FCSTD DOCUMENT  (FreeCAD 0.18R16146 (Git))
Label: main
License: All rights reserved
LicenseURL: http://en.wikipedia.org/wiki/All_rights_reserved
objects: Part::Feature×19, Part::Cylinder×14, Part::Cut×13, Part::Chamfer×7, Part::MultiFuse×2, Part::Box×2
note: 57 computed .brp shape members not serialized (recipe doc carries the construction recipe); baked Part::Feature solids carry a one-line shape summary decoded from their .brp

FEATURE [Part::Feature] Part__Feature071  label="MotorGear"
  Placement = pos=(-6.5467,-3.00361,17.9999) rot=(0,1,0;6.02251rad)
  shape: bbox 14.64 x 15 x 14.64 mm, 359 faces (baked)
FEATURE [Part::Feature] Part__Feature072  label="FlyGear"
  Placement = pos=(6.30321,-3.05009,17.9985) rot=(0,-1,0;4.705rad)
  shape: bbox 15.15 x 20 x 15.15 mm, 372 faces (baked)
FEATURE [Part::Feature] Part__Feature025  label="LatchSleve"
  shape: bbox 4 x 12 x 4 mm, 4 faces (baked)
FEATURE [Part::Feature] Part__Feature004  label="LatchShaft"
  Placement = pos=(9.90321,14.3499,6.99894) rot=(0.999993,0.00265,-0.00265;1.5708rad)
  shape: bbox 3.247 x 20 x 3.247 mm, 5 faces (baked)
FEATURE [Part::Feature] Fusion001001  label="asembly-shaft"
  Placement = pos=(-6.555,-4.85,18) rot=(1,0,0;4.71239rad)
  shape: bbox 25.99 x 28 x 26 mm, 508 faces (baked)
FEATURE [Part::Feature] Part__Feature056001001001  label="bearing"
  Placement = pos=(-6.555,-3.5,18) rot=(1,0,0;1.5708rad)
  shape: bbox 8 x 2.5 x 8 mm, 12 faces (baked)
FEATURE [Part::Feature] Part__Feature056001001002  label="bearing001"
  Placement = pos=(-6.325,22.5,18) rot=(1,0,0;1.5708rad)
  shape: bbox 8 x 2.5 x 8 mm, 12 faces (baked)
FEATURE [Part::Feature] Fusion001002001  label="Fusion003"
  Placement = pos=(6,4.47,30.5) rot=(0,1,0;1.5708rad)
  shape: bbox 22.5 x 12.1 x 12.1 mm, 188 faces (baked)
FEATURE [Part::Feature] Part__Feature028  label="insert M3 v1"
  Placement = pos=(3.65321,4.45,30.4999) rot=(-0.57735,-0.57735,-0.57735;2.0944rad)
  shape: bbox 5.909 x 4.726 x 4.72 mm, 153 faces (baked)
FEATURE [Part::Feature] Part__Feature006  label="T10 SpurGear"
  Placement = pos=(3.9913e-08,-1.44113e-07,9e-15) rot=(0,0,1;0.017453rad)
  shape: bbox 6 x 5.817 x 5.76 mm, 83 faces (baked)
FEATURE [Part::Feature] Fusion001002002001003  label="name14"
  shape: bbox 50.3 x 39.95 x 23 mm, 596 faces (baked)
FEATURE [Part::MultiFuse] Fusion  label="moto-with-gear"
  Placement = pos=(0,17.1,32) rot=(-0.935113,0.250563,0.250563;1.63783rad)
  Shapes = -> [Part__Feature006,Fusion001002002001003]
FEATURE [Part::Feature] Fusion001  label="motor-cut"
  Placement = pos=(0,7.1e-15,32) rot=(1,0,0;4.71239rad)
  shape: bbox 47.04 x 10 x 16.2 mm, 9 faces, 3 solids (baked)
FEATURE [Part::Box] Box  label="Cube"
  AttacherType = Attacher::AttachEngine3D
  Height = 25
  Length = 51
  Placement = pos=(-26,0,12) rot=(0,0,1;0rad)
  Width = 10
FEATURE [Part::Cylinder] Cylinder
  Angle = 360
  AttacherType = Attacher::AttachEngine3D
  Height = 10
  Placement = pos=(-6.325,-2.85,18) rot=(-1,0,0;1.5708rad)
  Radius = 17
FEATURE [Part::Cylinder] Cylinder001
  Angle = 360
  AttacherType = Attacher::AttachEngine3D
  Height = 10
  Placement = pos=(-6.325,8e-15,18) rot=(-1,0,0;1.5708rad)
  Radius = 3.25
FEATURE [Part::Cylinder] Cylinder002
  Angle = 360
  AttacherType = Attacher::AttachEngine3D
  Height = 10
  Placement = pos=(-6.325,-0.45,18) rot=(-1,0,0;1.5708rad)
  Radius = 4.1
FEATURE [Part::Cut] Cut
  Base = -> Box
  Tool = -> Cylinder
FEATURE [Part::Cut] Cut001
  Base = -> Cut
  Tool = -> Cylinder002
FEATURE [Part::Cut] Cut002
  Base = -> Cut001
  Tool = -> Cylinder001
FEATURE [Part::Chamfer] Chamfer
  Base = -> Cut002
  Edges = 1 edges r=0.5: [Edge25]
FEATURE [Part::Chamfer] Chamfer001
  Base = -> Chamfer
  Edges = 2 edges r=3: [Edge26,Edge27]
FEATURE [Part::Box] Box001  label="Cube001"
  AttacherType = Attacher::AttachEngine3D
  Height = 15
  Length = 14
  Placement = pos=(12,0,12) rot=(0,0,1;0rad)
  Width = 10
FEATURE [Part::Cut] Cut003
  Base = -> Chamfer001
  Tool = -> Box001
FEATURE [Part::Cut] Cut004  label="320-aligner-test"
  Base = -> Cut003
  Tool = -> Fusion001
FEATURE [Part::Feature] Common001001  label="back-plate-base"
  Placement = pos=(0,15,32) rot=(0.935113,-0.250563,-0.250563;4.64535rad)
  shape: bbox 44.17 x 8 x 36 mm, 14 faces (baked)
FEATURE [Part::Cylinder] Cylinder003
  Angle = 360
  AttacherType = Attacher::AttachEngine3D
  Height = 8
  Placement = pos=(-6.325,23,18) rot=(1,0,0;1.5708rad)
  Radius = 16
FEATURE [Part::Feature] Part__Feature056001001002001  label="bearing002"
  shape: bbox 8 x 2.5 x 8 mm, 12 faces (baked)
FEATURE [Part::Feature] Fusion001001001  label="asembly-shaft001"
  Placement = pos=(0.2,0,0) rot=(0,0,1;0rad)
  shape: bbox 25.99 x 28 x 26 mm, 508 faces (baked)
FEATURE [Part::Feature] Part__Feature056001001001001  label="bearing003"
  Placement = pos=(0.2,0,0) rot=(0,0,1;0rad)
  shape: bbox 8 x 2.5 x 8 mm, 12 faces (baked)
FEATURE [Part::Feature] Part__Feature071001  label="MotorGear001"
  Placement = pos=(0.2,0,0) rot=(0,0,1;0rad)
  shape: bbox 14.64 x 15 x 14.64 mm, 359 faces (baked)
FEATURE [Part::Cylinder] Cylinder004
  Angle = 360
  AttacherType = Attacher::AttachEngine3D
  Height = 7
  Placement = pos=(-6.325,20.5,18) rot=(1,0,0;1.5708rad)
  Radius = 14
FEATURE [Part::Chamfer] Chamfer002
  Base = -> Cylinder003
  Edges = 1 edges r=2: [Edge3]
FEATURE [Part::Cylinder] Cylinder006
  Angle = 360
  AttacherType = Attacher::AttachEngine3D
  Height = 10
  Placement = pos=(-6.325,23,18) rot=(1,0,0;1.5708rad)
  Radius = 3.25
FEATURE [Part::Cylinder] Cylinder007
  Angle = 360
  AttacherType = Attacher::AttachEngine3D
  Height = 10
  Placement = pos=(-6.325,22.5,18) rot=(1,0,0;1.5708rad)
  Radius = 4.1
FEATURE [Part::Cylinder] Cylinder008
  Angle = 360
  AttacherType = Attacher::AttachEngine3D
  Height = 10
  Placement = pos=(-19,10,0) rot=(0,0,1;0rad)
  Radius = 2
FEATURE [Part::Cylinder] Cylinder009
  Angle = 360
  AttacherType = Attacher::AttachEngine3D
  Height = 10
  Placement = pos=(19.5,10,0) rot=(0,0,1;0rad)
  Radius = 2
FEATURE [Part::Cylinder] Cylinder010  label="filament"
  Angle = 360
  AttacherType = Attacher::AttachEngine3D
  Height = 60
  Placement = pos=(0,9,0) rot=(0,0,1;0rad)
  Radius = 0.9
FEATURE [Part::Cylinder] Cylinder011
  Angle = 360
  AttacherType = Attacher::AttachEngine3D
  Height = 10
  Placement = pos=(0,20,32) rot=(1,0,0;1.5708rad)
  Radius = 27.1
FEATURE [Part::Cut] Cut005
  Base = -> Common001001
  Tool = -> Cylinder011
FEATURE [Part::Cylinder] Cylinder012
  Angle = 142
  AttacherType = Attacher::AttachEngine3D
  Height = 10
  Placement = pos=(0,23,32) rot=(0.990855,0.095409,-0.095409;1.57998rad)
  Radius = 26
FEATURE [Part::Cylinder] Cylinder013
  Angle = 360
  AttacherType = Attacher::AttachEngine3D
  Height = 10
  Placement = pos=(0,23,32) rot=(1,0,0;1.5708rad)
  Radius = 12
FEATURE [Part::Feature] Fusion001002002001004  label="motor-cut001"
  Placement = pos=(0,23,32) rot=(-0.935113,-0.250563,0.250563;4.64535rad)
  shape: bbox 41.07 x 10 x 25.02 mm, 9 faces, 3 solids (baked)
FEATURE [Part::Cut] Cut006
  Base = -> Cylinder012
  Tool = -> Cylinder013
FEATURE [Part::Cut] Cut007
  Base = -> Cut005
  Tool = -> Cut006
FEATURE [Part::Chamfer] Chamfer003
  Base = -> Cut007
  Edges = 2 edges r=1: [Edge39,Edge41]
FEATURE [Part::Chamfer] Chamfer004
  Base = -> Chamfer003
  Edges = 17 edges r=0.4: [Edge19,Edge23,Edge25,Edge27,Edge29,Edge30,Edge33,Edge35,Edge36,Edge39,Edge40,Edge43,Edge45,Edge47,Edge48,Edge50,Edge52]
FEATURE [Part::Cut] Cut008
  Base = -> Chamfer004
  Tool = -> Fusion001002002001004
FEATURE [Part::Chamfer] Chamfer005
  Base = -> Cut008
  Edges = 1 edges r=0.4: [Edge52]
FEATURE [Part::Cylinder] Cylinder014
  Angle = 360
  AttacherType = Attacher::AttachEngine3D
  Height = 10
  Placement = pos=(0,23,32) rot=(1,0,0;1.5708rad)
  Radius = 8.5
FEATURE [Part::Cut] Cut009
  Base = -> Chamfer002
  Tool = -> Cylinder014
FEATURE [Part::Chamfer] Chamfer006
  Base = -> Cut009
  Edges = 2 edges r=1: [Edge2,Edge9]
FEATURE [Part::MultiFuse] Fusion001002002001005
  Shapes = -> [Chamfer005,Chamfer006]
FEATURE [Part::Cut] Cut010
  Base = -> Fusion001002002001005
  Tool = -> Cylinder004
FEATURE [Part::Cut] Cut011
  Base = -> Cut010
  Tool = -> Cylinder007
FEATURE [Part::Cut] Cut012
  Base = -> Cut011
  Tool = -> Cylinder006
FEATURE [Part::Feature] Part__Feature  label="Latch"
  Placement = pos=(-6.34679,-10.5501,18) rot=(1,0,0;3.14159rad)
  shape: bbox 20.03 x 24 x 38.43 mm, 141 faces (baked)
